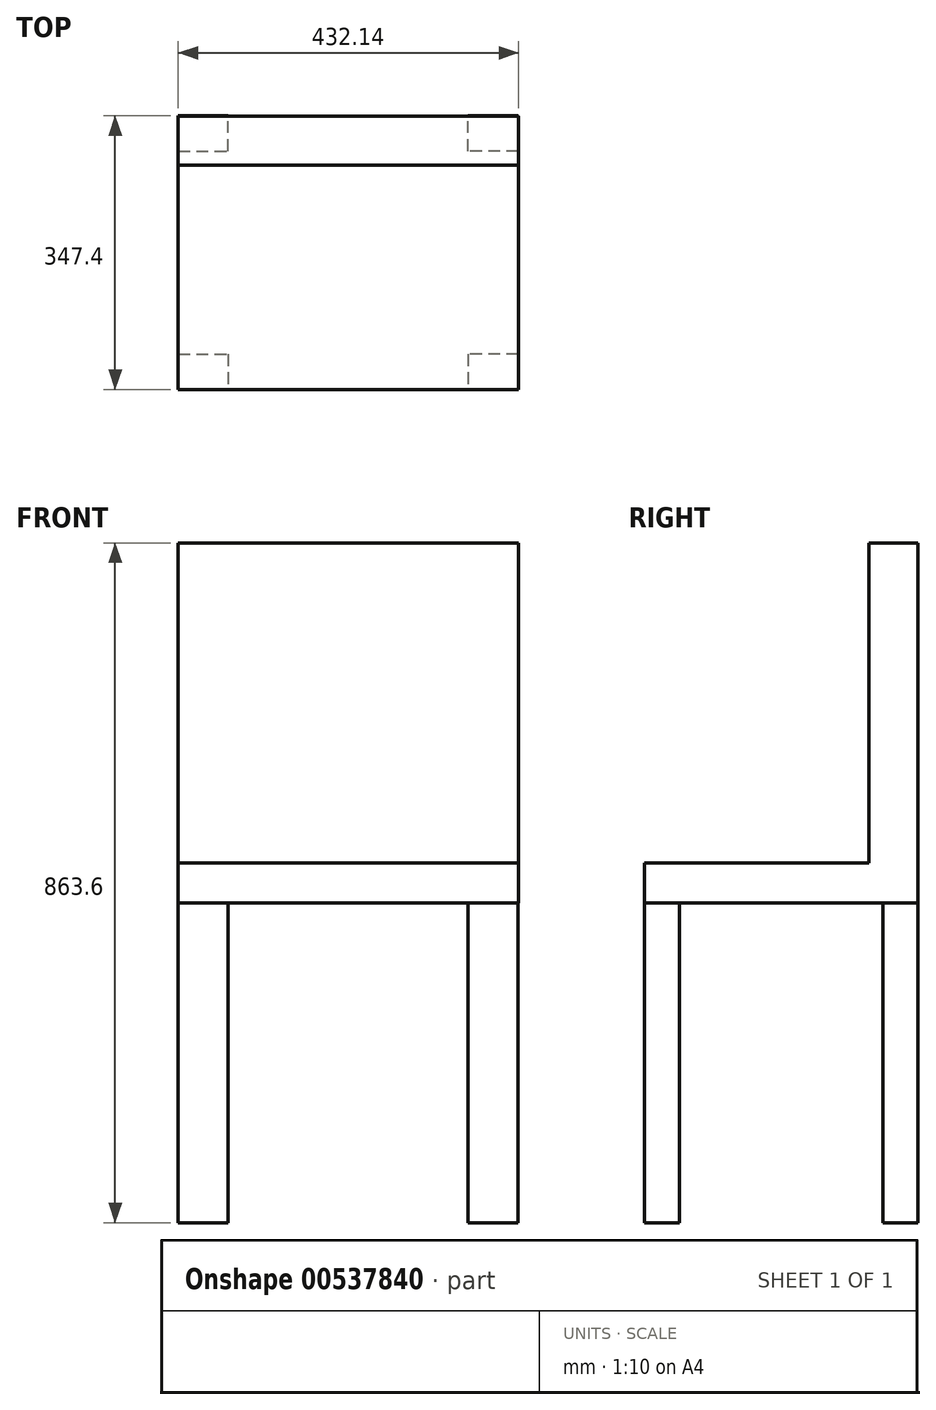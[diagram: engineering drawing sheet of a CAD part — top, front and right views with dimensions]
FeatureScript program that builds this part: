
annotation { "Feature Type Name" : "Feature", "Feature Type Description" : "" }
export const myFeature = defineFeature(function(context is Context, id is Id, definition is map)
    precondition{}
    {
        {
            var Q0;
            Q0=qCreatedBy(makeId("Top.planeOp"),FACE);
            var sketch = newSketch(context, id + "F0", { "sketchPlane" : qUnion([Q0])});
            skLineSegment(sketch, "E0.top", {"start": v(0, 0) * mm, "end": v(63.5, 0) * mm});
            skLineSegment(sketch, "E0.left", {"start": v(0, 44.63) * mm, "end": v(0, 0) * mm});
            skLineSegment(sketch, "E0.right", {"start": v(63.5, 44.63) * mm, "end": v(63.5, 0) * mm});
            skLineSegment(sketch, "E1", {"start": v(63.5, 0) * mm, "end": v(368.3, 0) * mm});
            skLineSegment(sketch, "E2", {"start": v(0, 44.63) * mm, "end": v(63.5, 44.63) * mm});
            skLineSegment(sketch, "E3.MirrorCS", {"start": v(431.8, 44.63) * mm, "end": v(368.3, 44.63) * mm});
            skLineSegment(sketch, "E4.MirrorCS", {"start": v(431.8, 44.63) * mm, "end": v(431.8, 0) * mm});
            skLineSegment(sketch, "E5.MirrorCS", {"start": v(368.3, 44.63) * mm, "end": v(368.3, 0) * mm});
            skLineSegment(sketch, "E6.MirrorCS", {"start": v(431.8, 0) * mm, "end": v(431.8, 44.63) * mm});
            skLineSegment(sketch, "E7", {"start": v(215.9, 0) * mm, "end": v(215.9, 347.4) * mm});
            skLineSegment(sketch, "E8", {"start": v(368.3, 0) * mm, "end": v(431.8, 0) * mm});
            skLineSegment(sketch, "E9", {"start": v(215.9, 173.7) * mm, "end": v(62.05, 173.7) * mm});
            skPoint(sketch, "E9.endSnap0", {"position": v(215.9, 173.7) * mm});
            skLineSegment(sketch, "E10.MirrorCS", {"start": v(0, 302.77) * mm, "end": v(63.5, 302.77) * mm});
            skLineSegment(sketch, "E11.MirrorCS", {"start": v(0, 347.4) * mm, "end": v(63.5, 347.4) * mm});
            skLineSegment(sketch, "E12.MirrorCS", {"start": v(63.5, 302.77) * mm, "end": v(63.5, 347.4) * mm});
            skLineSegment(sketch, "E13.MirrorCS", {"start": v(0, 302.77) * mm, "end": v(0, 347.4) * mm});
            skLineSegment(sketch, "E14.MirrorCS", {"start": v(431.8, 302.77) * mm, "end": v(368.3, 302.77) * mm});
            skLineSegment(sketch, "E15.MirrorCS", {"start": v(368.3, 347.4) * mm, "end": v(431.8, 347.4) * mm});
            skLineSegment(sketch, "E16.MirrorCS", {"start": v(368.3, 302.77) * mm, "end": v(368.3, 347.4) * mm});
            skLineSegment(sketch, "E17.MirrorCS", {"start": v(431.8, 347.4) * mm, "end": v(431.8, 302.77) * mm});
            skSolve(sketch);
        }
        {
            var Q0;
            Q0 = qSketchRegion(id + "F0", true);
            extrude(context, id + "F1", {"entities" : qUnion([Q0]), "depth" : 406.4 * mm, "offsetDistance" : 25.4 * mm});
        }
        {
            var Q0;
            Q0=makeQuery(id+"F1.opExtrude","CAP_FACE",FACE,{"disambiguationData":[OSD([sQuery(id+"F0.wireOp",EDGE,"E0.top"),sQuery(id+"F0.wireOp",EDGE,"E0.left"),sQuery(id+"F0.wireOp",EDGE,"E0.right"),sQuery(id+"F0.wireOp",EDGE,"E2")])],"isStart":false});
            var sketch = newSketch(context, id + "F2", { "sketchPlane" : qUnion([Q0])});
            skLineSegment(sketch, "E18.bottom", {"start": v(0, 0) * mm, "end": v(432.14, 0) * mm});
            skLineSegment(sketch, "E18.top", {"start": v(0, 347.3) * mm, "end": v(432.14, 347.3) * mm});
            skLineSegment(sketch, "E18.left", {"start": v(0, 0) * mm, "end": v(0, 347.3) * mm});
            skLineSegment(sketch, "E18.right", {"start": v(432.14, 0) * mm, "end": v(432.14, 347.3) * mm});
            skSolve(sketch);
        }
        {
            var Q0;
            Q0 = qSketchRegion(id + "F2", true);
            extrude(context, id + "F3", {"entities" : qUnion([Q0]), "depth" : 50.8 * mm, "offsetDistance" : 25.4 * mm});
        }
        {
            var Q0;
            Q0=makeQuery(id+"F3.opExtrude","CAP_FACE",FACE,{"disambiguationData":[OSD([sQuery(id+"F2.wireOp",EDGE,"E18.bottom"),sQuery(id+"F2.wireOp",EDGE,"E18.top"),sQuery(id+"F2.wireOp",EDGE,"E18.left"),sQuery(id+"F2.wireOp",EDGE,"E18.right")])],"isStart":false});
            var sketch = newSketch(context, id + "F4", { "sketchPlane" : qUnion([Q0])});
            skLineSegment(sketch, "E19.bottom", {"start": v(0, 347.3) * mm, "end": v(432.14, 347.3) * mm});
            skLineSegment(sketch, "E19.top", {"start": v(0, 285) * mm, "end": v(432.14, 285) * mm});
            skLineSegment(sketch, "E19.left", {"start": v(0, 347.3) * mm, "end": v(0, 285) * mm});
            skLineSegment(sketch, "E19.right", {"start": v(432.14, 347.3) * mm, "end": v(432.14, 285) * mm});
            skSolve(sketch);
        }
        {
            var Q0;
            Q0 = qSketchRegion(id + "F4", true);
            extrude(context, id + "F5", {"entities" : qUnion([Q0]), "operationType" : NewBodyOperationType.ADD, "depth" : 406.4 * mm, "offsetDistance" : 25.4 * mm});
        }
    });
